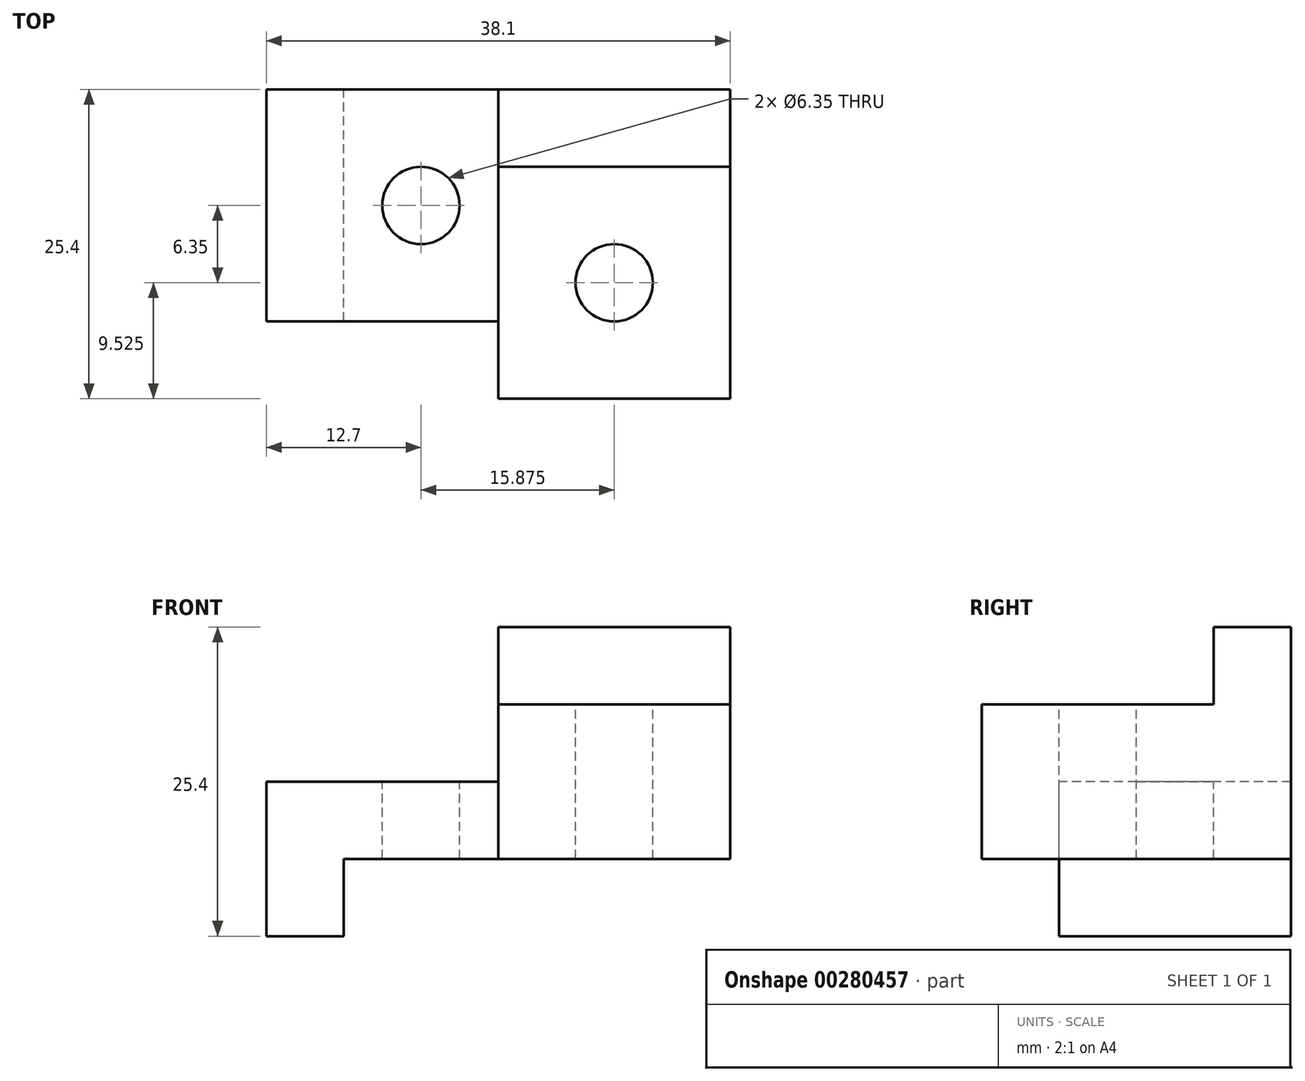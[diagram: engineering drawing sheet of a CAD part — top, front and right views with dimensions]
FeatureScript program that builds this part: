
annotation { "Feature Type Name" : "Feature", "Feature Type Description" : "" }
export const myFeature = defineFeature(function(context is Context, id is Id, definition is map)
    precondition{}
    {
        {
            var Q0;
            Q0=qCreatedBy(makeId("Top.planeOp"),FACE);
            var sketch = newSketch(context, id + "F0", { "sketchPlane" : qUnion([Q0])});
            skLineSegment(sketch, "E0.bottom", {"start": v(0, 0) * mm, "end": v(19.05, 0) * mm});
            skLineSegment(sketch, "E0.top", {"start": v(0, 25.4) * mm, "end": v(19.05, 25.4) * mm});
            skLineSegment(sketch, "E0.left", {"start": v(0, 0) * mm, "end": v(0, 25.4) * mm});
            skLineSegment(sketch, "E0.right", {"start": v(19.05, 0) * mm, "end": v(19.05, 25.4) * mm});
            skSolve(sketch);
        }
        {
            var Q0;
            Q0 = qSketchRegion(id + "F0", true);
            extrude(context, id + "F1", {"entities" : qUnion([Q0]), "depth" : 19.05 * mm});
        }
        {
            var Q0;
            Q0=makeQuery(id+"F1.opExtrude","CAP_FACE",FACE,{"disambiguationData":[OSD([sQuery(id+"F0.wireOp",EDGE,"E0.bottom"),sQuery(id+"F0.wireOp",EDGE,"E0.top"),sQuery(id+"F0.wireOp",EDGE,"E0.left"),sQuery(id+"F0.wireOp",EDGE,"E0.right")])],"isStart":false});
            var sketch = newSketch(context, id + "F2", { "sketchPlane" : qUnion([Q0])});
            skLineSegment(sketch, "E1.bottom", {"start": v(19.05, 0) * mm, "end": v(0, 0) * mm});
            skLineSegment(sketch, "E1.top", {"start": v(19.05, 19.05) * mm, "end": v(0, 19.05) * mm});
            skLineSegment(sketch, "E1.left", {"start": v(19.05, 0) * mm, "end": v(19.05, 19.05) * mm});
            skLineSegment(sketch, "E1.right", {"start": v(0, 0) * mm, "end": v(0, 19.05) * mm});
            skSolve(sketch);
        }
        {
            var Q0;
            Q0 = qSketchRegion(id + "F2", true);
            extrude(context, id + "F3", {"entities" : qUnion([Q0]), "operationType" : NewBodyOperationType.REMOVE, "oppositeDirection" : true, "depth" : 6.35 * mm});
        }
        {
            var Q0;
            Q0=makeQuery(id+"F3.boolean.opBoolean","COPY",FACE,{"derivedFrom":makeQuery(id+"F3.opExtrude","CAP_FACE",FACE,{"disambiguationData":[OSD([sQuery(id+"F2.wireOp",EDGE,"E1.bottom"),sQuery(id+"F2.wireOp",EDGE,"E1.top"),sQuery(id+"F2.wireOp",EDGE,"E1.left"),sQuery(id+"F2.wireOp",EDGE,"E1.right")])],"isStart":false})});
            var sketch = newSketch(context, id + "F4", { "sketchPlane" : qUnion([Q0])});
            skCircle(sketch, "E2", {"center": v(9.53, 9.52) * mm, "radius": 3.18 * mm});
            skSolve(sketch);
        }
        {
            var Q0;
            Q0 = qSketchRegion(id + "F4", true);
            extrude(context, id + "F5", {"entities" : qUnion([Q0]), "operationType" : NewBodyOperationType.REMOVE, "endBound" : BoundingType.THROUGH_ALL, "oppositeDirection" : true, "depth" : 25.4 * mm});
        }
        {
            var Q0;
            Q0=makeQuery(id+"F1.opExtrude","SWEPT_FACE",FACE,{"disambiguationData":[OSD([sQuery(id+"F0.wireOp",EDGE,"E0.left")])]});
            var sketch = newSketch(context, id + "F6", { "sketchPlane" : qUnion([Q0])});
            skLineSegment(sketch, "E3.bottom", {"start": v(-25.4, 0) * mm, "end": v(-6.35, 0) * mm});
            skLineSegment(sketch, "E3.top", {"start": v(-25.4, 6.35) * mm, "end": v(-6.35, 6.35) * mm});
            skLineSegment(sketch, "E3.left", {"start": v(-25.4, 0) * mm, "end": v(-25.4, 6.35) * mm});
            skLineSegment(sketch, "E3.right", {"start": v(-6.35, 0) * mm, "end": v(-6.35, 6.35) * mm});
            skSolve(sketch);
        }
        {
            var Q0;
            Q0 = qSketchRegion(id + "F6", true);
            extrude(context, id + "F7", {"entities" : qUnion([Q0]), "operationType" : NewBodyOperationType.ADD, "depth" : 19.05 * mm});
        }
        {
            var Q0;
            Q0=makeQuery(id+"F7.boolean.opBoolean","MERGE",FACE,{"derivedFrom":[makeQuery(id+"F1.opExtrude","CAP_FACE",FACE,{"disambiguationData":[OSD([sQuery(id+"F0.wireOp",EDGE,"E0.bottom"),sQuery(id+"F0.wireOp",EDGE,"E0.top"),sQuery(id+"F0.wireOp",EDGE,"E0.left"),sQuery(id+"F0.wireOp",EDGE,"E0.right")])],"isStart":true}),makeQuery(id+"F7.opExtrude","SWEPT_FACE",FACE,{"disambiguationData":[OSD([sQuery(id+"F6.wireOp",EDGE,"E3.bottom")])]})]});
            var sketch = newSketch(context, id + "F8", { "sketchPlane" : qUnion([Q0])});
            skLineSegment(sketch, "E4.bottom", {"start": v(-19.05, -6.35) * mm, "end": v(-12.7, -6.35) * mm});
            skLineSegment(sketch, "E4.top", {"start": v(-19.05, -25.4) * mm, "end": v(-12.7, -25.4) * mm});
            skLineSegment(sketch, "E4.left", {"start": v(-19.05, -6.35) * mm, "end": v(-19.05, -25.4) * mm});
            skLineSegment(sketch, "E4.right", {"start": v(-12.7, -6.35) * mm, "end": v(-12.7, -25.4) * mm});
            skSolve(sketch);
        }
        {
            var Q0;
            Q0 = qSketchRegion(id + "F8", true);
            extrude(context, id + "F9", {"entities" : qUnion([Q0]), "operationType" : NewBodyOperationType.ADD, "depth" : 6.35 * mm});
        }
        {
            var Q0;
            Q0=makeQuery(id+"F7.opExtrude","SWEPT_FACE",FACE,{"disambiguationData":[OSD([sQuery(id+"F6.wireOp",EDGE,"E3.top")])]});
            var sketch = newSketch(context, id + "F10", { "sketchPlane" : qUnion([Q0])});
            skCircle(sketch, "E5", {"center": v(-6.35, 15.88) * mm, "radius": 3.18 * mm});
            skLineSegment(sketch, "E6", {"start": v(0, 6.35) * mm, "end": v(-6.35, 6.35) * mm});
            skLineSegment(sketch, "E7", {"start": v(0, 6.35) * mm, "end": v(0, 15.88) * mm});
            skSolve(sketch);
        }
        {
            var Q0;
            Q0 = qSketchRegion(id + "F10", true);
            extrude(context, id + "F11", {"entities" : qUnion([Q0]), "operationType" : NewBodyOperationType.REMOVE, "endBound" : BoundingType.THROUGH_ALL, "oppositeDirection" : true, "depth" : 25.4 * mm});
        }
    });
